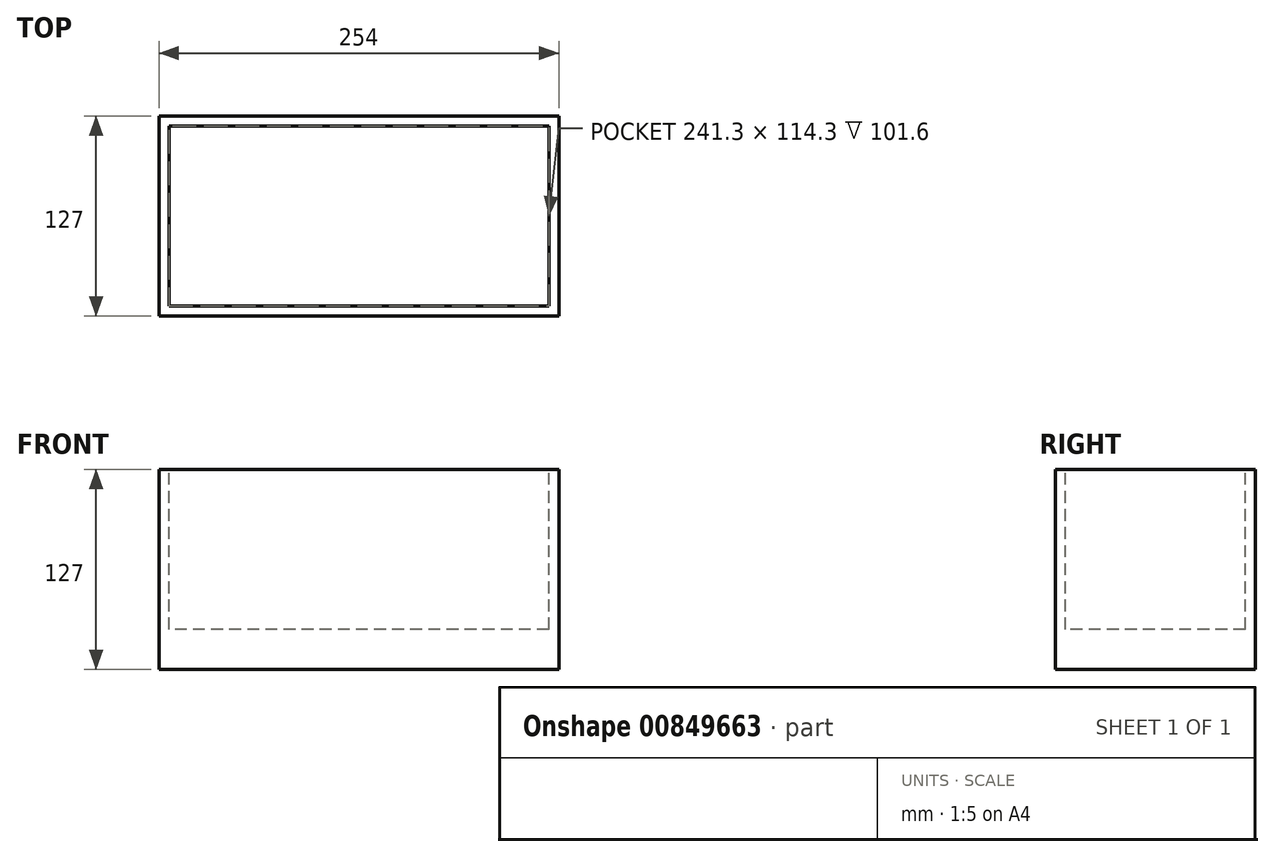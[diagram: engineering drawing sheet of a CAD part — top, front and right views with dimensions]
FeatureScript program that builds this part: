
annotation { "Feature Type Name" : "Feature", "Feature Type Description" : "" }
export const myFeature = defineFeature(function(context is Context, id is Id, definition is map)
    precondition{}
    {
        {
            var Q0;
            Q0=qCreatedBy(makeId("Top.planeOp"),FACE);
            var sketch = newSketch(context, id + "F0", { "sketchPlane" : qUnion([Q0])});
            skLineSegment(sketch, "E0", {"start": v(0, 0) * mm, "end": v(25.4, 0) * mm, "construction": true});
            skLineSegment(sketch, "E1.bottom", {"start": v(152.4, 63.5) * mm, "end": v(-101.6, 63.5) * mm});
            skLineSegment(sketch, "E1.top", {"start": v(152.4, -63.5) * mm, "end": v(-101.6, -63.5) * mm});
            skLineSegment(sketch, "E1.left", {"start": v(152.4, 63.5) * mm, "end": v(152.4, -63.5) * mm});
            skLineSegment(sketch, "E1.right", {"start": v(-101.6, 63.5) * mm, "end": v(-101.6, -63.5) * mm});
            skPoint(sketch, "E1.middle", {"position": v(25.4, 0) * mm});
            skSolve(sketch);
        }
        {
            var Q0;
            Q0=makeQuery(id+"F0.imprint","IMPRINT",FACE,{"disambiguationData":[TD([[makeQuery(id+"F0.imprint","IMPRINT",EDGE,{"derivedFrom":sQuery(id+"F0.wireOp",EDGE,"E1.bottom")}),1.0]])]});
            extrude(context, id + "F1", {"entities" : qUnion([Q0]), "depth" : 38.1 * mm, "offsetDistance" : 25.4 * mm});
        }
        {
            var Q0;
            Q0=makeQuery(id+"F1.opExtrude","CAP_FACE",FACE,{"disambiguationData":[OSD([sQuery(id+"F0.wireOp",EDGE,"E1.bottom"),sQuery(id+"F0.wireOp",EDGE,"E1.top"),sQuery(id+"F0.wireOp",EDGE,"E1.left"),sQuery(id+"F0.wireOp",EDGE,"E1.right")])],"isStart":true});
            var Q1;
            Q1 = qSketchRegion(id + "F0", true);
            extrude(context, id + "F2", {"entities" : qUnion([Q0, Q1]), "operationType" : NewBodyOperationType.ADD, "depth" : 88.9 * mm, "offsetDistance" : 25.4 * mm});
        }
        {
            var Q0;
            Q0=makeQuery(id+"F1.opExtrude","CAP_FACE",FACE,{"disambiguationData":[OSD([sQuery(id+"F0.wireOp",EDGE,"E1.bottom"),sQuery(id+"F0.wireOp",EDGE,"E1.top"),sQuery(id+"F0.wireOp",EDGE,"E1.left"),sQuery(id+"F0.wireOp",EDGE,"E1.right")])],"isStart":false});
            var sketch = newSketch(context, id + "F3", { "sketchPlane" : qUnion([Q0])});
            skLineSegment(sketch, "E2.0", {"start": v(146.05, -57.15) * mm, "end": v(-95.25, -57.15) * mm});
            skLineSegment(sketch, "E2.1", {"start": v(146.05, 57.15) * mm, "end": v(146.05, -57.15) * mm});
            skLineSegment(sketch, "E2.2", {"start": v(146.05, 57.15) * mm, "end": v(-95.25, 57.15) * mm});
            skLineSegment(sketch, "E2.3", {"start": v(-95.25, 57.15) * mm, "end": v(-95.25, -57.15) * mm});
            skSolve(sketch);
        }
        {
            var Q0;
            Q0 = qSketchRegion(id + "F3", true);
            extrude(context, id + "F4", {"entities" : qUnion([Q0]), "operationType" : NewBodyOperationType.REMOVE, "oppositeDirection" : true, "depth" : 101.6 * mm, "offsetDistance" : 25.4 * mm});
        }
    });
